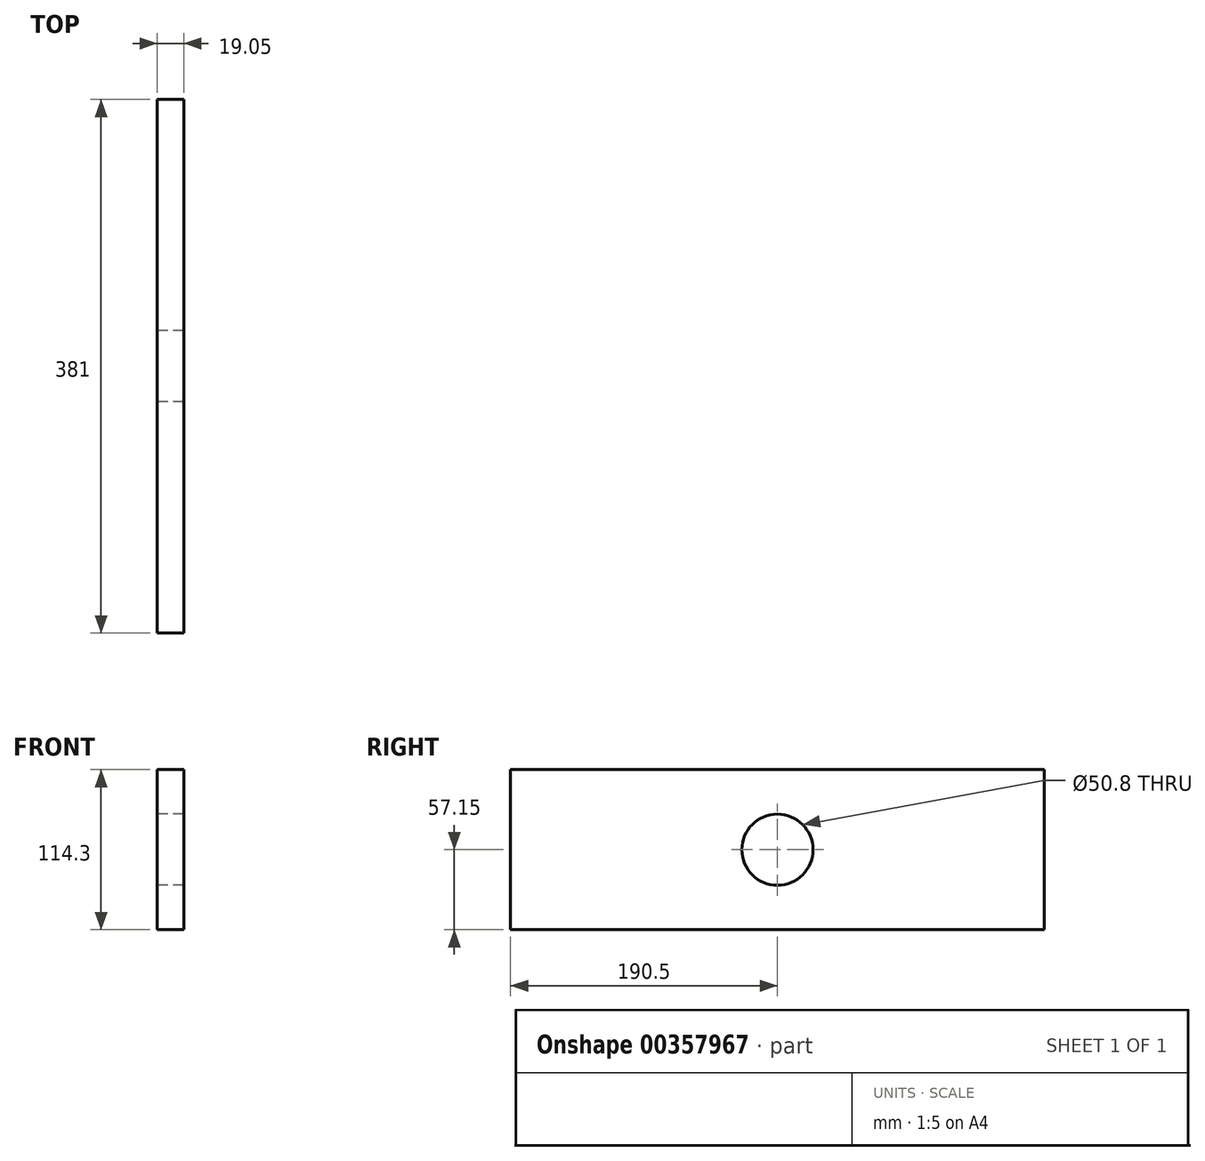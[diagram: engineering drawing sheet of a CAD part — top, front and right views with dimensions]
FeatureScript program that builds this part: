
annotation { "Feature Type Name" : "Feature", "Feature Type Description" : "" }
export const myFeature = defineFeature(function(context is Context, id is Id, definition is map)
    precondition{}
    {
        {
            var Q0;
            Q0=qCreatedBy(makeId("Right.planeOp"),FACE);
            var sketch = newSketch(context, id + "F0", { "sketchPlane" : qUnion([Q0])});
            skLineSegment(sketch, "E0.bottom", {"start": v(190.5, -57.15) * mm, "end": v(-190.5, -57.15) * mm});
            skLineSegment(sketch, "E0.top", {"start": v(190.5, 57.15) * mm, "end": v(-190.5, 57.15) * mm});
            skLineSegment(sketch, "E0.left", {"start": v(190.5, -57.15) * mm, "end": v(190.5, 57.15) * mm});
            skLineSegment(sketch, "E0.right", {"start": v(-190.5, -57.15) * mm, "end": v(-190.5, 57.15) * mm});
            skPoint(sketch, "E0.middle", {"position": v(0, 0) * mm});
            skCircle(sketch, "E1", {"center": v(0, 0) * mm, "radius": 25.4 * mm});
            skSolve(sketch);
        }
        {
            var Q0;
            Q0=makeQuery(id+"F0.imprint","IMPRINT",FACE,{"disambiguationData":[TD([[makeQuery(id+"F0.imprint","IMPRINT",EDGE,{"derivedFrom":sQuery(id+"F0.wireOp",EDGE,"E0.bottom")}),-1.0]])]});
            extrude(context, id + "F1", {"entities" : qUnion([Q0]), "depth" : 19.05 * mm});
        }
    });
